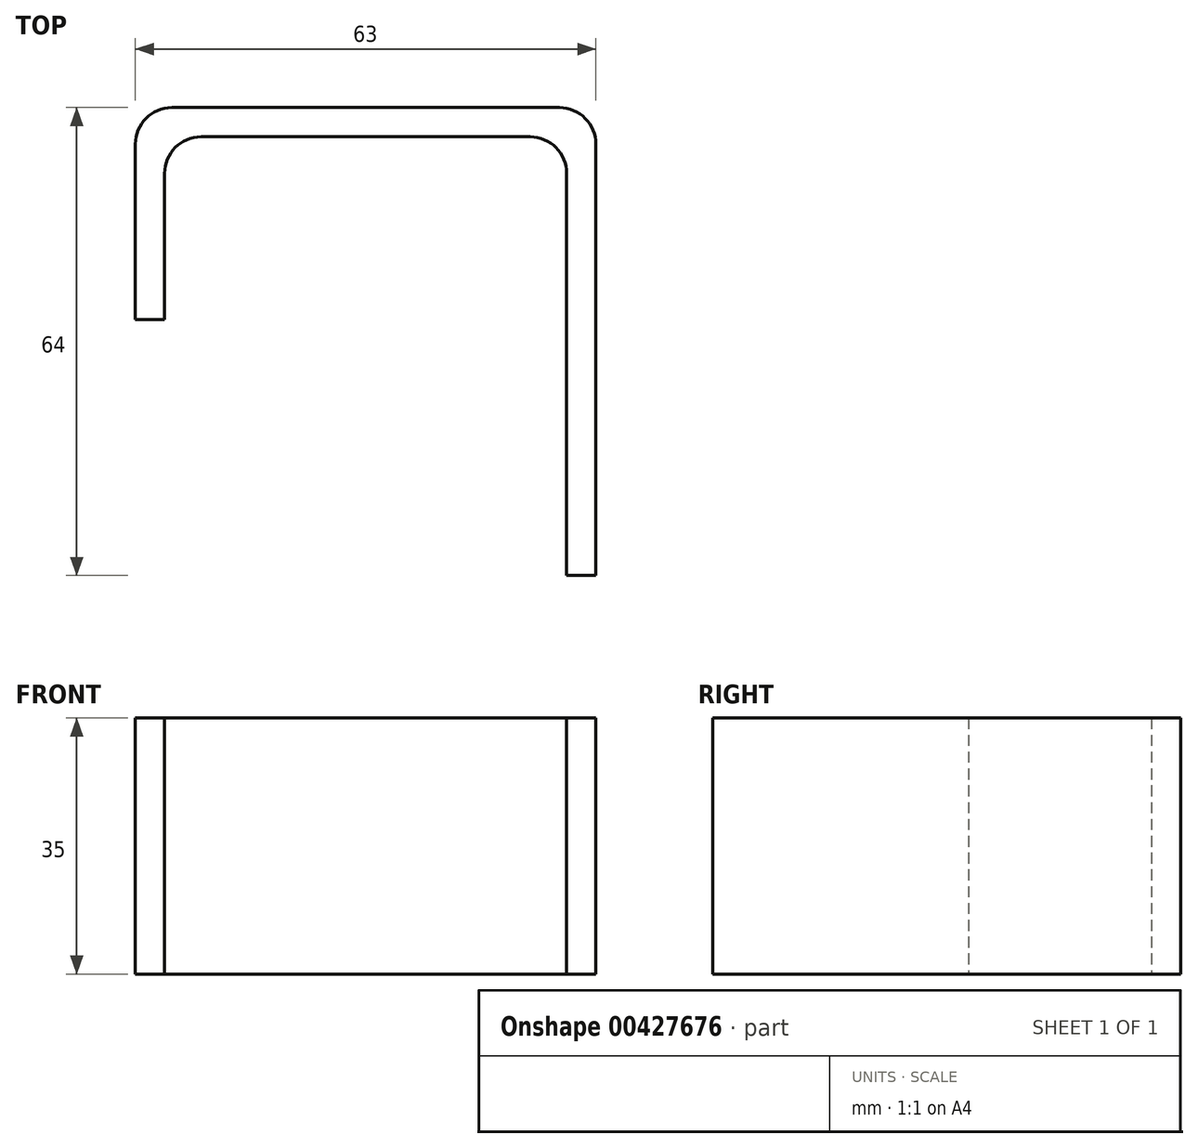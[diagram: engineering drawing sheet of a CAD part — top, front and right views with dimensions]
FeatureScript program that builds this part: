
annotation { "Feature Type Name" : "Feature", "Feature Type Description" : "" }
export const myFeature = defineFeature(function(context is Context, id is Id, definition is map)
    precondition{}
    {
        {
            var Q0;
            Q0=qCreatedBy(makeId("Top.planeOp"),FACE);
            var sketch = newSketch(context, id + "F0", { "sketchPlane" : qUnion([Q0])});
            skLineSegment(sketch, "E0", {"start": v(-14.22, 11.34) * mm, "end": v(30.78, 11.34) * mm});
            skLineSegment(sketch, "E1", {"start": v(-19.22, 6.34) * mm, "end": v(-19.22, -13.66) * mm});
            skLineSegment(sketch, "E2", {"start": v(35.78, 6.34) * mm, "end": v(35.78, -48.66) * mm});
            skLineSegment(sketch, "E3.0", {"start": v(-23.22, 10.34) * mm, "end": v(-23.22, -13.66) * mm});
            skLineSegment(sketch, "E3.1", {"start": v(-18.22, 15.34) * mm, "end": v(34.78, 15.34) * mm});
            skLineSegment(sketch, "E3.2", {"start": v(39.78, 10.34) * mm, "end": v(39.78, -48.66) * mm});
            skLineSegment(sketch, "E4", {"start": v(-23.22, -13.66) * mm, "end": v(-19.22, -13.66) * mm});
            skLineSegment(sketch, "E5", {"start": v(35.78, -48.66) * mm, "end": v(39.78, -48.66) * mm});
            skPoint(sketch, "E6.visualSharp", {"position": v(-19.22, 11.34) * mm});
            skArc(sketch, "E6.filletArc", {"start": v(-14.22, 11.34) * mm, "mid": v(-17.76, 9.88) * mm, "end": v(-19.22, 6.34) * mm});
            skPoint(sketch, "E7.visualSharp", {"position": v(35.78, 11.34) * mm});
            skArc(sketch, "E7.filletArc", {"start": v(35.78, 6.34) * mm, "mid": v(34.31, 9.88) * mm, "end": v(30.78, 11.34) * mm});
            skPoint(sketch, "E8.visualSharp", {"position": v(-23.22, 15.34) * mm});
            skArc(sketch, "E8.filletArc", {"start": v(-18.22, 15.34) * mm, "mid": v(-21.76, 13.88) * mm, "end": v(-23.22, 10.34) * mm});
            skPoint(sketch, "E9.visualSharp", {"position": v(39.78, 15.34) * mm});
            skArc(sketch, "E9.filletArc", {"start": v(39.78, 10.34) * mm, "mid": v(38.31, 13.88) * mm, "end": v(34.78, 15.34) * mm});
            skSolve(sketch);
        }
        {
            var Q0;
            Q0=makeQuery(id+"F0.imprint","IMPRINT",FACE,{"disambiguationData":[TD([[makeQuery(id+"F0.imprint","IMPRINT",EDGE,{"derivedFrom":sQuery(id+"F0.wireOp",EDGE,"E0")}),1.0]])]});
            extrude(context, id + "F1", {"entities" : qUnion([Q0]), "depth" : 35 * mm});
        }
    });
